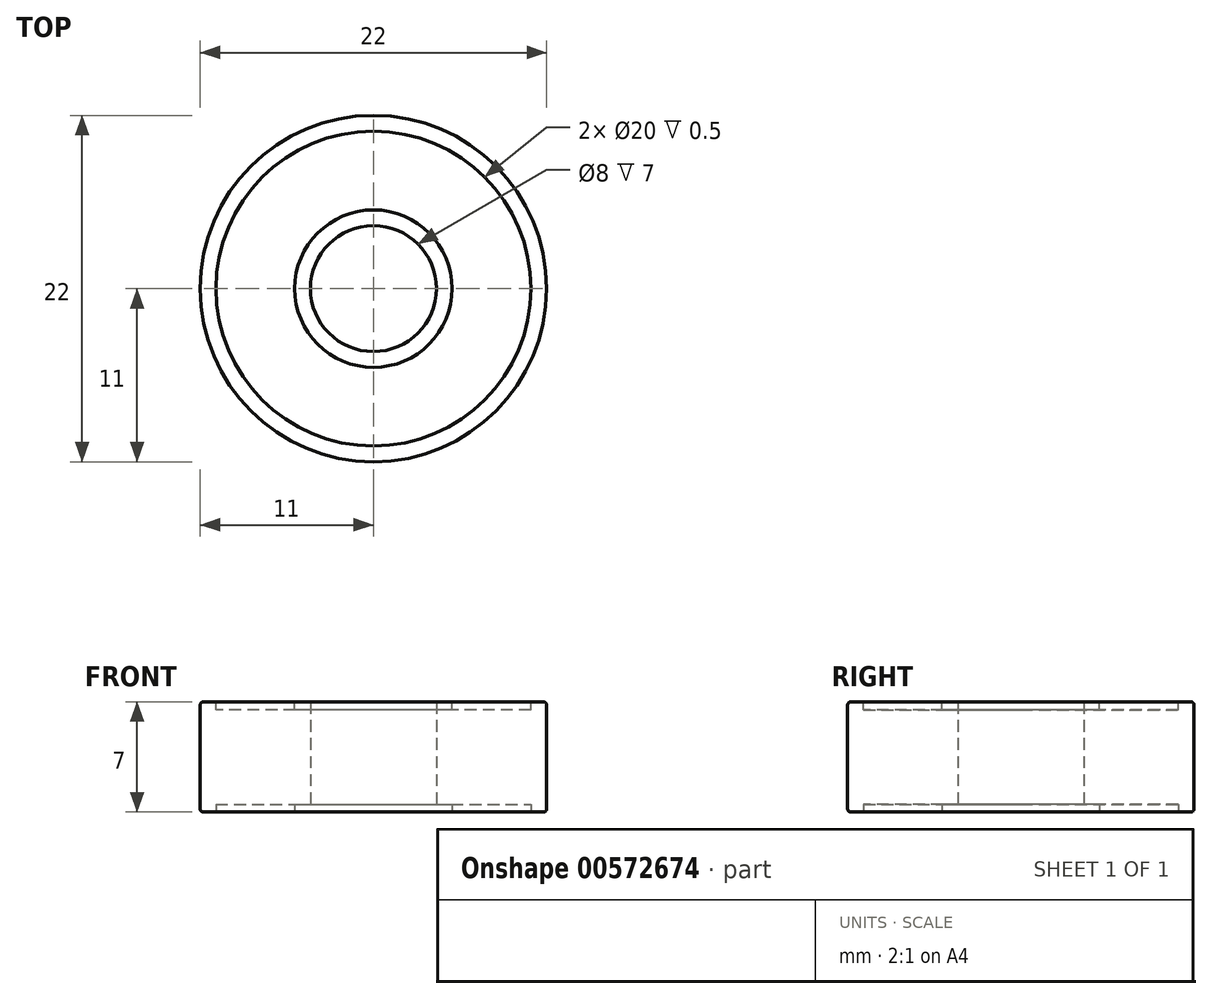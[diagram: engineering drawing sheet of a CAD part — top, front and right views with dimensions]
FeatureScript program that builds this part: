
annotation { "Feature Type Name" : "Feature", "Feature Type Description" : "" }
export const myFeature = defineFeature(function(context is Context, id is Id, definition is map)
    precondition{}
    {
        {
            var Q0;
            Q0=qCreatedBy(makeId("Top.planeOp"),FACE);
            var sketch = newSketch(context, id + "F0", { "sketchPlane" : qUnion([Q0])});
            skCircle(sketch, "E0", {"center": v(0, 0) * mm, "radius": 11 * mm});
            skCircle(sketch, "E1", {"center": v(0, 0) * mm, "radius": 4 * mm});
            skSolve(sketch);
        }
        {
            var Q0;
            Q0=qSketchRegion(id+"F0",true);
            extrude(context, id + "F1", {"entities" : qUnion([Q0]), "depth" : 7 * mm, "offsetDistance" : 25 * mm});
        }
        {
            var Q0;
            Q0=makeQuery(id+"F1.opExtrude","CAP_FACE",FACE,{"disambiguationData":[OSD([sQuery(id+"F0.wireOp",EDGE,"E0"),sQuery(id+"F0.wireOp",EDGE,"E1")])],"isStart":false});
            var sketch = newSketch(context, id + "F2", { "sketchPlane" : qUnion([Q0])});
            skCircle(sketch, "E2.0", {"center": v(0, 0) * mm, "radius": 4 * mm, "construction": true});
            skCircle(sketch, "E3.0", {"center": v(0, 0) * mm, "radius": 11 * mm, "construction": true});
            skCircle(sketch, "E4.0", {"center": v(0, 0) * mm, "radius": 10 * mm});
            skCircle(sketch, "E5.0", {"center": v(0, 0) * mm, "radius": 5 * mm});
            skSolve(sketch);
        }
        {
            var Q0;
            Q0=qSketchRegion(id+"F2",true);
            extrude(context, id + "F3", {"entities" : qUnion([Q0]), "operationType" : NewBodyOperationType.REMOVE, "oppositeDirection" : true, "depth" : 0.5 * mm, "offsetDistance" : 25 * mm});
        }
        {
            var Q0;
            Q0=makeQuery(id+"F1.opExtrude","CAP_FACE",FACE,{"disambiguationData":[OSD([sQuery(id+"F0.wireOp",EDGE,"E0"),sQuery(id+"F0.wireOp",EDGE,"E1")])],"isStart":true});
            var sketch = newSketch(context, id + "F4", { "sketchPlane" : qUnion([Q0])});
            skCircle(sketch, "E6.0", {"center": v(0, 0) * mm, "radius": 11 * mm, "construction": true});
            skCircle(sketch, "E7.0", {"center": v(0, 0) * mm, "radius": 4 * mm, "construction": true});
            skCircle(sketch, "E8.0", {"center": v(0, 0) * mm, "radius": 10 * mm});
            skCircle(sketch, "E9.0", {"center": v(0, 0) * mm, "radius": 5 * mm});
            skSolve(sketch);
        }
        {
            var Q0;
            Q0=qSketchRegion(id+"F4",true);
            extrude(context, id + "F5", {"entities" : qUnion([Q0]), "operationType" : NewBodyOperationType.REMOVE, "oppositeDirection" : true, "depth" : 0.5 * mm, "offsetDistance" : 25 * mm});
        }
        {
            var Q0;
            Q0=makeQuery(id+"F1.opExtrude","CAP_EDGE",EDGE,{"disambiguationData":[OSD([sQuery(id+"F0.wireOp",EDGE,"E0")])],"isStart":true});
            var Q1;
            Q1=makeQuery(id+"F1.opExtrude","CAP_EDGE",EDGE,{"disambiguationData":[OSD([sQuery(id+"F0.wireOp",EDGE,"E0")])],"isStart":false});
            fillet(context, id + "F6", {"entities" : qUnion([Q0, Q1]), "radius" : 0.2 * mm, "tangentPropagation" : true, "allowEdgeOverflow" : false});
        }
    });
